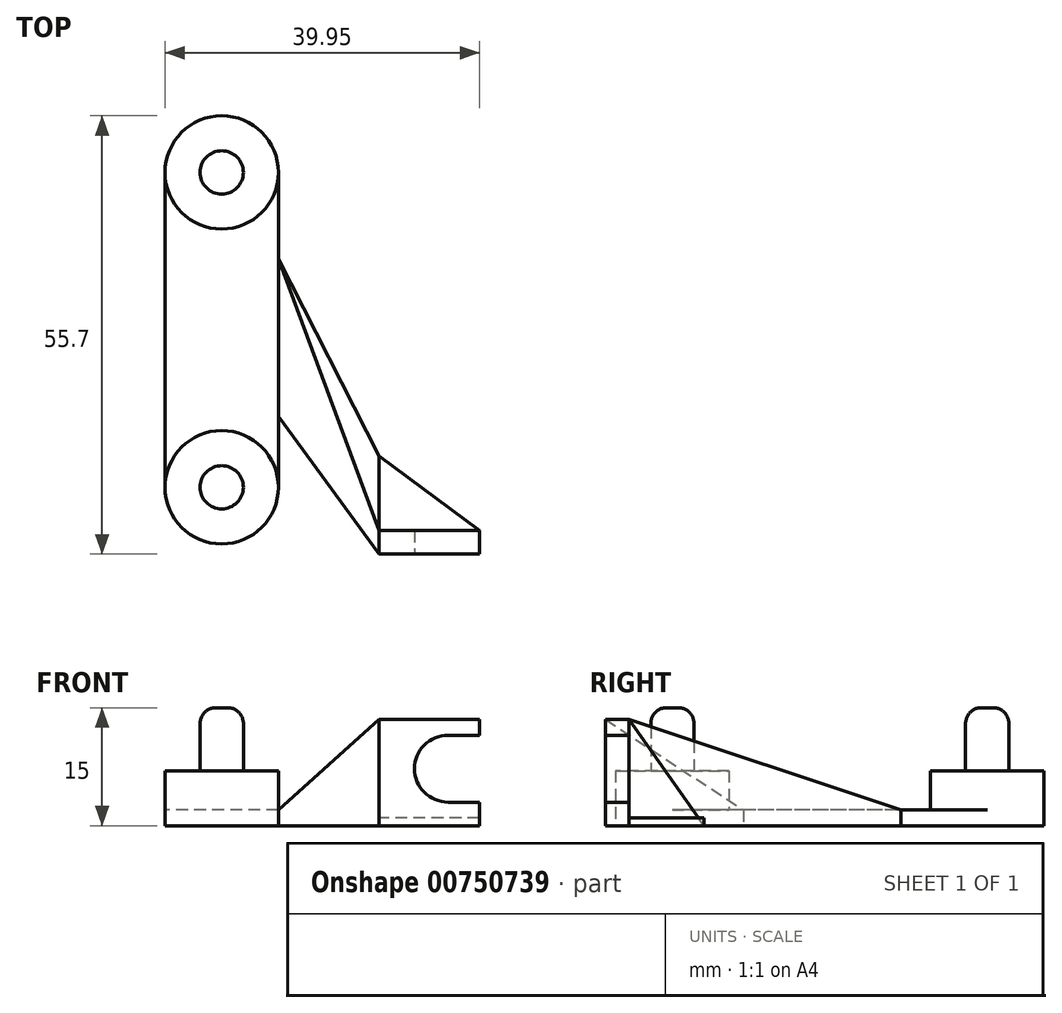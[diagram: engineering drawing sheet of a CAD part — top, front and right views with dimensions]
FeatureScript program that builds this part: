
annotation { "Feature Type Name" : "Feature", "Feature Type Description" : "" }
export const myFeature = defineFeature(function(context is Context, id is Id, definition is map)
    precondition{}
    {
        {
            var Q0;
            Q0=qCreatedBy(makeId("Top.planeOp"),FACE);
            var sketch = newSketch(context, id + "F0", { "sketchPlane" : qUnion([Q0])});
            skLineSegment(sketch, "E0", {"start": v(0, 20) * mm, "end": v(0, -20) * mm, "construction": true});
            skPoint(sketch, "E1", {"position": v(0, 0) * mm});
            skCircle(sketch, "E2", {"center": v(0, 20) * mm, "radius": 2.9 * mm, "construction": true});
            skCircle(sketch, "E3", {"center": v(0, -20) * mm, "radius": 2.9 * mm, "construction": true});
            skLineSegment(sketch, "E4", {"start": v(-7.2, 20) * mm, "end": v(-7.2, -20) * mm});
            skLineSegment(sketch, "E5", {"start": v(7.2, 20) * mm, "end": v(7.2, -20) * mm});
            skArc(sketch, "E6", {"start": v(-7.2, -20) * mm, "mid": v(0, -27.2) * mm, "end": v(7.2, -20) * mm});
            skArc(sketch, "E7", {"start": v(7.2, -20) * mm, "mid": v(0, -12.8) * mm, "end": v(-7.2, -20) * mm, "construction": true});
            skArc(sketch, "E8", {"start": v(-7.2, 20) * mm, "mid": v(0, 12.8) * mm, "end": v(7.2, 20) * mm, "construction": true});
            skArc(sketch, "E9", {"start": v(7.2, 20) * mm, "mid": v(0, 27.2) * mm, "end": v(-7.2, 20) * mm});
            skSolve(sketch);
        }
        {
            var Q0;
            Q0 = qSketchRegion(id + "F0", true);
            extrude(context, id + "F1", {"entities" : qUnion([Q0]), "depth" : 2 * mm, "offsetDistance" : 25 * mm});
        }
        {
            var Q0;
            Q0=makeQuery(id+"F1.opExtrude","CAP_FACE",FACE,{"disambiguationData":[OSD([sQuery(id+"F0.wireOp",EDGE,"E4"),sQuery(id+"F0.wireOp",EDGE,"E5"),sQuery(id+"F0.wireOp",EDGE,"E6"),sQuery(id+"F0.wireOp",EDGE,"E9")])],"isStart":false});
            var sketch = newSketch(context, id + "F2", { "sketchPlane" : qUnion([Q0])});
            skCircle(sketch, "E10", {"center": v(0, 20) * mm, "radius": 2.75 * mm});
            skCircle(sketch, "E11", {"center": v(0, -20) * mm, "radius": 2.75 * mm});
            skSolve(sketch);
        }
        {
            var Q0;
            Q0 = qSketchRegion(id + "F2", true);
            extrude(context, id + "F3", {"entities" : qUnion([Q0]), "operationType" : NewBodyOperationType.ADD, "depth" : 13 * mm, "offsetDistance" : 25 * mm});
        }
        {
            var Q0;
            Q0=qCreatedBy(makeId("Front.planeOp"),FACE);
            cPlane(context, id + "F4", {"entities" : qUnion([Q0]), "cplaneType" : CPlaneType.OFFSET, "offset" : 28.5 * mm, "width" : 150 * mm, "height" : 150 * mm});
        }
        {
            var Q0;
            Q0=qCreatedBy(id+"F4.planeOp",FACE);
            var sketch = newSketch(context, id + "F5", { "sketchPlane" : qUnion([Q0])});
            skLineSegment(sketch, "E12.bottom", {"start": v(32.75, 0) * mm, "end": v(20, 0) * mm});
            skLineSegment(sketch, "E12.top", {"start": v(32.75, 13.5) * mm, "end": v(20, 13.5) * mm});
            skLineSegment(sketch, "E12.left", {"start": v(32.75, 0) * mm, "end": v(32.75, 3) * mm});
            skLineSegment(sketch, "E12.right", {"start": v(20, 0) * mm, "end": v(20, 13.5) * mm});
            skLineSegment(sketch, "E13", {"start": v(32.75, 11.5) * mm, "end": v(28.75, 11.5) * mm});
            skLineSegment(sketch, "E14", {"start": v(32.75, 3) * mm, "end": v(28.75, 3) * mm});
            skArc(sketch, "E15", {"start": v(28.75, 11.5) * mm, "mid": v(24.5, 7.25) * mm, "end": v(28.75, 3) * mm});
            skLineSegment(sketch, "E16.trimOffspring", {"start": v(32.75, 11.5) * mm, "end": v(32.75, 13.5) * mm});
            skCircle(sketch, "E17", {"center": v(28.75, 7.25) * mm, "radius": 5.5 * mm, "construction": true});
            skSolve(sketch);
        }
        {
            var Q0;
            Q0 = qSketchRegion(id + "F5", true);
            extrude(context, id + "F6", {"entities" : qUnion([Q0]), "operationType" : NewBodyOperationType.ADD, "oppositeDirection" : true, "depth" : 3 * mm, "offsetDistance" : 25 * mm});
        }
        {
            var Q0;
            Q0=makeQuery(id+"F6.opExtrude","SWEPT_FACE",FACE,{"disambiguationData":[OSD([sQuery(id+"F5.wireOp",EDGE,"E12.right")])]});
            var sketch = newSketch(context, id + "F7", { "sketchPlane" : qUnion([Q0])});
            skLineSegment(sketch, "E18.top", {"start": v(28.5, 0) * mm, "end": v(16, 0) * mm});
            skLineSegment(sketch, "E18.left", {"start": v(28.5, 13.5) * mm, "end": v(28.5, 0) * mm});
            skLineSegment(sketch, "E19", {"start": v(16, 0) * mm, "end": v(25.5, 13.5) * mm});
            skLineSegment(sketch, "E20.0", {"start": v(25.5, 13.5) * mm, "end": v(28.5, 13.5) * mm});
            skSolve(sketch);
        }
        {
            var Q0;
            Q0=makeQuery(id+"F1.opExtrude","SWEPT_FACE",FACE,{"disambiguationData":[OSD([sQuery(id+"F0.wireOp",EDGE,"E5")])]});
            var sketch = newSketch(context, id + "F8", { "sketchPlane" : qUnion([Q0])});
            skLineSegment(sketch, "E21.0", {"start": v(20, 2) * mm, "end": v(-20, 2) * mm});
            skLineSegment(sketch, "E21.1", {"start": v(20, 0) * mm, "end": v(-20, 0) * mm});
            skLineSegment(sketch, "E22", {"start": v(-11, 2) * mm, "end": v(-11, 0) * mm});
            skLineSegment(sketch, "E23", {"start": v(9, 2) * mm, "end": v(9, 0) * mm});
            skSolve(sketch);
        }
        {
            var Q0;
            Q0 = qSketchRegion(id + "F7", true);
            var Q1;
            Q1 = qSketchRegion(id + "F8", true);
            var Q2;
            Q2=sQuery(id+"F7.wireOp",VERTEX,"E18.top.end");
            var Q3;
            Q3=sQuery(id+"F8.wireOp",VERTEX,"E23.end");
            loft(context, id + "F9", {"operationType" : NewBodyOperationType.ADD, "sheetProfilesArray" : [{ "sheetProfileEntities" : qUnion([Q0]) }, { "sheetProfileEntities" : qUnion([Q1]) }], "matchConnections" : true, "connections" : [{ "connectionEntities" : qUnion([Q2, Q3]), "connectionEdgeQueries" : qUnion([]), "connectionEdgeParameters" : [] }]});
        }
        {
            var Q0;
            {var subQ0=sQuery(id+"F0.wireOp",EDGE,"E9");var subQ1=sQuery(id+"F0.wireOp",EDGE,"E5");Q0=makeQuery(id+"F9.boolean.opBoolean","MERGE",FACE,{"derivedFrom":[makeQuery(id+"F1.opExtrude","CAP_FACE",FACE,{"disambiguationData":[OSD([sQuery(id+"F0.wireOp",EDGE,"E4"),subQ1,sQuery(id+"F0.wireOp",EDGE,"E6"),subQ0])],"isStart":true}),makeQuery(id+"F6.opExtrude","SWEPT_FACE",FACE,{"disambiguationData":[OSD([sQuery(id+"F5.wireOp",EDGE,"E12.bottom")])]}),makeQuery(id+"F9.opLoft","SWEPT_FACE",FACE,{"disambiguationData":[OSD([subQ1,subQ0,sQuery(id+"F5.wireOp",EDGE,"E12.right"),sQuery(id+"F7.wireOp",EDGE,"E18.top"),sQuery(id+"F7.wireOp",EDGE,"E19"),sQuery(id+"F8.wireOp",EDGE,"E21.1")])]})]});}
            var sketch = newSketch(context, id + "F10", { "sketchPlane" : qUnion([Q0])});
            skLineSegment(sketch, "E24.1", {"start": v(32.75, 25.5) * mm, "end": v(20, 25.5) * mm});
            skLineSegment(sketch, "E25.0", {"start": v(20, 16) * mm, "end": v(20, 25.5) * mm});
            skLineSegment(sketch, "E26.0", {"start": v(20, 25.5) * mm, "end": v(20, 16) * mm});
            skLineSegment(sketch, "E27", {"start": v(20, 16) * mm, "end": v(32.75, 25.5) * mm});
            skSolve(sketch);
        }
        {
            var Q0;
            Q0 = qSketchRegion(id + "F10", true);
            extrude(context, id + "F11", {"entities" : qUnion([Q0]), "operationType" : NewBodyOperationType.ADD, "oppositeDirection" : true, "depth" : 1 * mm, "offsetDistance" : 25 * mm});
        }
        {
            var Q0;
            Q0=makeQuery(id+"F1.opExtrude","CAP_FACE",FACE,{"disambiguationData":[OSD([sQuery(id+"F0.wireOp",EDGE,"E4"),sQuery(id+"F0.wireOp",EDGE,"E5"),sQuery(id+"F0.wireOp",EDGE,"E6"),sQuery(id+"F0.wireOp",EDGE,"E9")])],"isStart":false});
            var sketch = newSketch(context, id + "F12", { "sketchPlane" : qUnion([Q0])});
            skArc(sketch, "E28.0", {"start": v(-7.2, 20) * mm, "mid": v(0, 12.8) * mm, "end": v(7.2, 20) * mm});
            skArc(sketch, "E28.1", {"start": v(7.2, 20) * mm, "mid": v(0, 27.2) * mm, "end": v(-7.2, 20) * mm});
            skArc(sketch, "E28.2", {"start": v(7.2, -20) * mm, "mid": v(0, -12.8) * mm, "end": v(-7.2, -20) * mm});
            skArc(sketch, "E28.3", {"start": v(-7.2, -20) * mm, "mid": v(0, -27.2) * mm, "end": v(7.2, -20) * mm});
            skSolve(sketch);
        }
        {
            var Q0;
            Q0 = qSketchRegion(id + "F12", true);
            extrude(context, id + "F13", {"entities" : qUnion([Q0]), "operationType" : NewBodyOperationType.ADD, "depth" : 5 * mm, "offsetDistance" : 25 * mm});
        }
        {
            var Q0;
            Q0=makeQuery(id+"F3.opExtrude","CAP_EDGE",EDGE,{"disambiguationData":[OSD([sQuery(id+"F2.wireOp",EDGE,"E10")])],"isStart":false});
            var Q1;
            Q1=makeQuery(id+"F3.opExtrude","CAP_EDGE",EDGE,{"disambiguationData":[OSD([sQuery(id+"F2.wireOp",EDGE,"E11")])],"isStart":false});
            fillet(context, id + "F14", {"entities" : qUnion([Q0, Q1]), "radius" : 2 * mm, "tangentPropagation" : true, "allowEdgeOverflow" : false});
        }
    });
